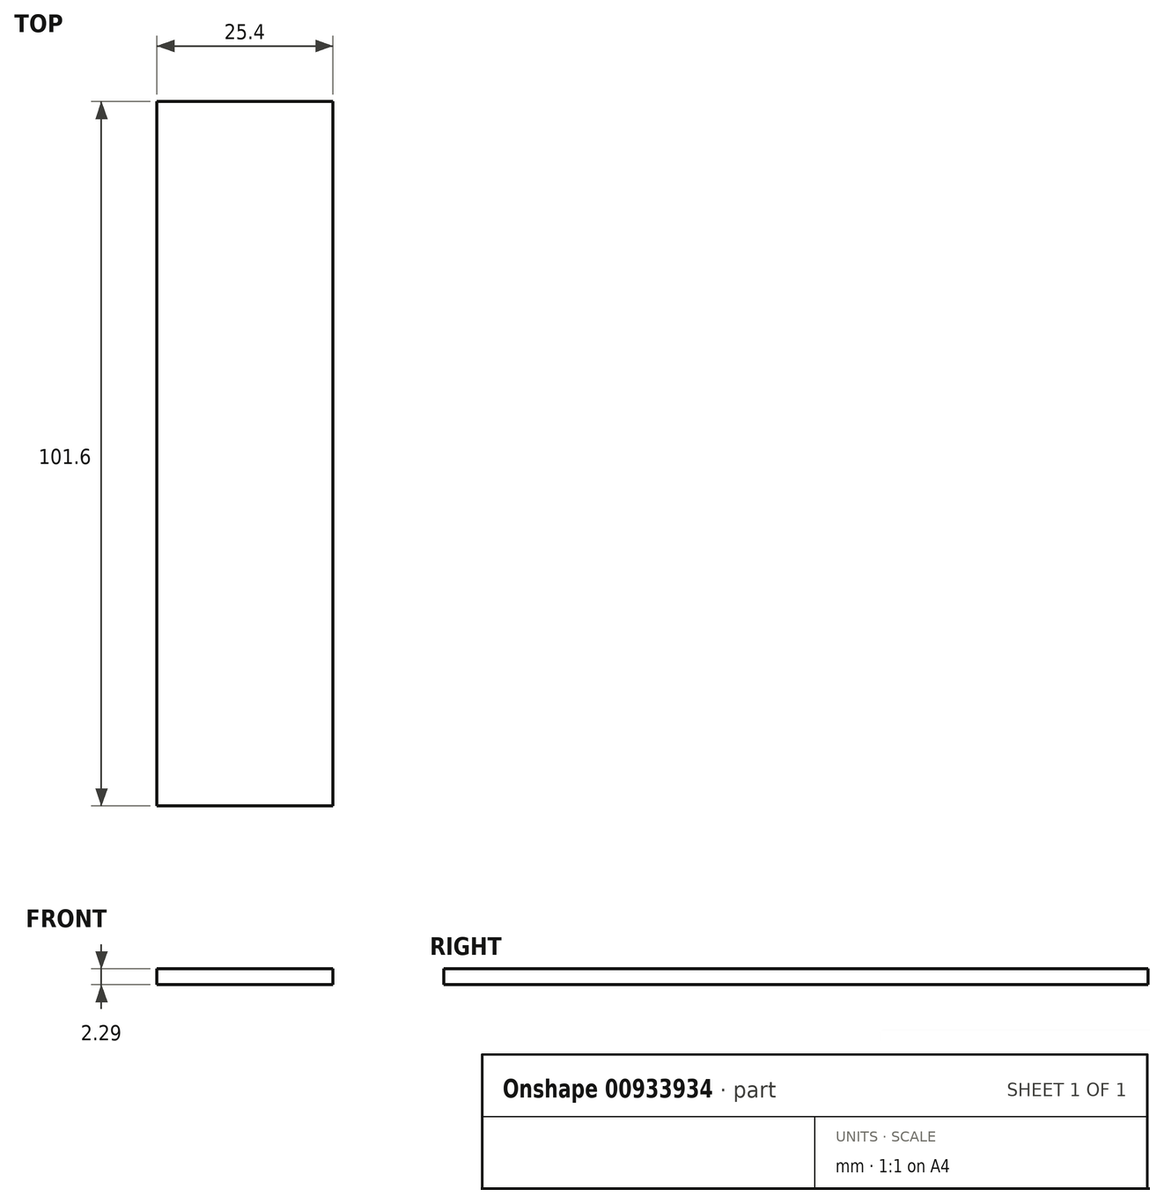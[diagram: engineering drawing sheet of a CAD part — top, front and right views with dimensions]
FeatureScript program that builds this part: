
annotation { "Feature Type Name" : "Feature", "Feature Type Description" : "" }
export const myFeature = defineFeature(function(context is Context, id is Id, definition is map)
    precondition{}
    {
        {
            var Q0;
            Q0=qCreatedBy(makeId("Top.planeOp"),FACE);
            var sketch = newSketch(context, id + "F0", { "sketchPlane" : qUnion([Q0])});
            skLineSegment(sketch, "E0.bottom", {"start": v(0, 0) * mm, "end": v(25.4, 0) * mm});
            skLineSegment(sketch, "E0.top", {"start": v(0, 101.6) * mm, "end": v(25.4, 101.6) * mm});
            skLineSegment(sketch, "E0.left", {"start": v(0, 0) * mm, "end": v(0, 101.6) * mm});
            skLineSegment(sketch, "E0.right", {"start": v(25.4, 0) * mm, "end": v(25.4, 101.6) * mm});
            skSolve(sketch);
        }
        {
            var Q0;
            Q0=makeQuery(id+"F0.imprint","IMPRINT",FACE,{"disambiguationData":[TD([[makeQuery(id+"F0.imprint","IMPRINT",EDGE,{"derivedFrom":sQuery(id+"F0.wireOp",EDGE,"E0.bottom")}),1.0]])]});
            extrude(context, id + "F1", {"entities" : qUnion([Q0]), "depth" : 2.3 * mm, "offsetDistance" : 25.4 * mm});
        }
    });
